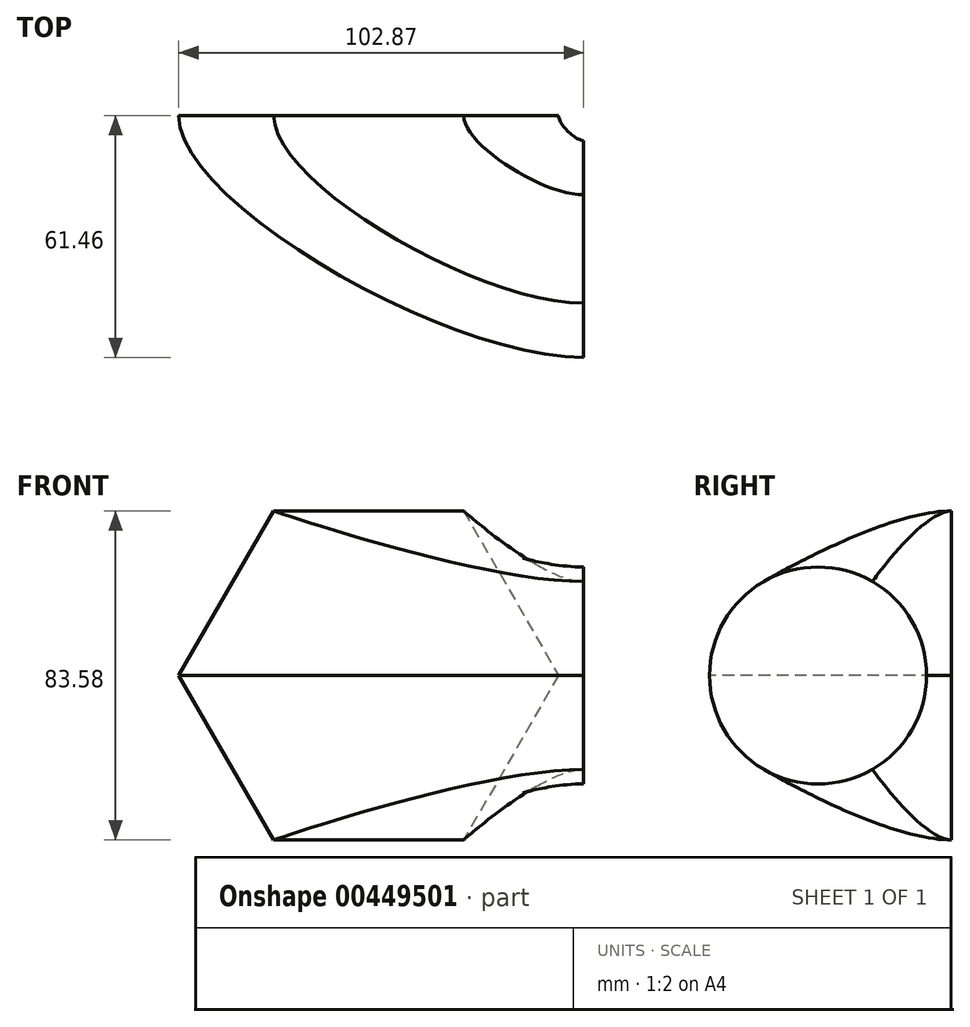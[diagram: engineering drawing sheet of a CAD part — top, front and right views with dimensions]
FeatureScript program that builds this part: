
annotation { "Feature Type Name" : "Feature", "Feature Type Description" : "" }
export const myFeature = defineFeature(function(context is Context, id is Id, definition is map)
    precondition{}
    {
        {
            var Q0;
            Q0=qCreatedBy(makeId("Front.planeOp"),FACE);
            var sketch = newSketch(context, id + "F0", { "sketchPlane" : qUnion([Q0])});
            skLineSegment(sketch, "E0", {"start": v(0, 0) * mm, "end": v(-54.61, 0) * mm, "construction": true});
            skCircle(sketch, "E1.cCircle", {"center": v(-54.61, 0) * mm, "radius": 41.8 * mm, "construction": true});
            skLineSegment(sketch, "E1.0", {"start": v(-78.74, 41.8) * mm, "end": v(-30.48, 41.8) * mm});
            skLineSegment(sketch, "E1.1", {"start": v(-30.48, 41.8) * mm, "end": v(-6.35, 0) * mm});
            skLineSegment(sketch, "E1.2", {"start": v(-6.35, 0) * mm, "end": v(-30.48, -41.8) * mm});
            skLineSegment(sketch, "E1.3", {"start": v(-30.48, -41.8) * mm, "end": v(-78.74, -41.8) * mm});
            skLineSegment(sketch, "E1.4", {"start": v(-78.74, -41.8) * mm, "end": v(-102.87, 0) * mm});
            skLineSegment(sketch, "E1.5", {"start": v(-102.87, 0) * mm, "end": v(-78.74, 41.8) * mm});
            skPoint(sketch, "E1.0.midPoint", {"position": v(-54.61, 41.8) * mm});
            skSolve(sketch);
        }
        {
            var Q0;
            Q0=qCreatedBy(makeId("Right.planeOp"),FACE);
            var sketch = newSketch(context, id + "F1", { "sketchPlane" : qUnion([Q0])});
            skLineSegment(sketch, "E2", {"start": v(0, 0) * mm, "end": v(-33.9, 0) * mm, "construction": true});
            skCircle(sketch, "E3.cCircle", {"center": v(-33.9, 0) * mm, "radius": 23.86 * mm, "construction": true});
            skLineSegment(sketch, "E3.0", {"start": v(-6.35, 0) * mm, "end": v(-20.13, -23.86) * mm, "construction": true});
            skLineSegment(sketch, "E3.1", {"start": v(-20.13, -23.86) * mm, "end": v(-47.68, -23.86) * mm, "construction": true});
            skLineSegment(sketch, "E3.2", {"start": v(-47.68, -23.86) * mm, "end": v(-61.46, 0) * mm, "construction": true});
            skLineSegment(sketch, "E3.3", {"start": v(-61.46, 0) * mm, "end": v(-47.68, 23.86) * mm, "construction": true});
            skLineSegment(sketch, "E3.4", {"start": v(-47.68, 23.86) * mm, "end": v(-20.13, 23.86) * mm, "construction": true});
            skLineSegment(sketch, "E3.5", {"start": v(-20.13, 23.86) * mm, "end": v(-6.35, 0) * mm, "construction": true});
            skPoint(sketch, "E3.0.midPoint", {"position": v(-13.24, -11.93) * mm});
            skArc(sketch, "E4", {"start": v(-20.13, -23.86) * mm, "mid": v(-10.04, 13.78) * mm, "end": v(-47.68, 23.86) * mm});
            skArc(sketch, "E5", {"start": v(-47.68, -23.86) * mm, "mid": v(-33.9, -27.55) * mm, "end": v(-20.13, -23.86) * mm});
            skArc(sketch, "E6", {"start": v(-61.46, 0) * mm, "mid": v(-57.76, -13.78) * mm, "end": v(-47.68, -23.86) * mm});
            skArc(sketch, "E7", {"start": v(-47.68, 23.86) * mm, "mid": v(-57.76, 13.78) * mm, "end": v(-61.46, 0) * mm});
            skSolve(sketch);
        }
        {
            var Q0;
            Q0=makeQuery(id+"F0.imprint","IMPRINT",FACE,{"disambiguationData":[TD([[makeQuery(id+"F0.imprint","IMPRINT",EDGE,{"derivedFrom":sQuery(id+"F0.wireOp",EDGE,"E1.0")}),-1.0]])]});
            var Q1;
            Q1=makeQuery(id+"F1.imprint","IMPRINT",FACE,{"disambiguationData":[TD([[makeQuery(id+"F1.imprint","IMPRINT",EDGE,{"derivedFrom":sQuery(id+"F1.wireOp",EDGE,"E4")}),1.0]])]});
            var Q2;
            Q2=sQuery(id+"F0.wireOp",VERTEX,"E1.1.end");
            var Q3;
            Q3=sQuery(id+"F1.wireOp",VERTEX,"E3.0.start");
            loft(context, id + "F2", {"startCondition" : LoftEndDerivativeType.NORMAL_TO_PROFILE, "startMagnitude" : 1, "endCondition" : LoftEndDerivativeType.NORMAL_TO_PROFILE, "endMagnitude" : 1, "sheetProfilesArray" : [{ "sheetProfileEntities" : qUnion([Q0]) }, { "sheetProfileEntities" : qUnion([Q1]) }], "matchConnections" : true, "connections" : [{ "connectionEntities" : qUnion([Q2, Q3]), "connectionEdgeQueries" : qUnion([]), "connectionEdgeParameters" : [] }]});
        }
    });
